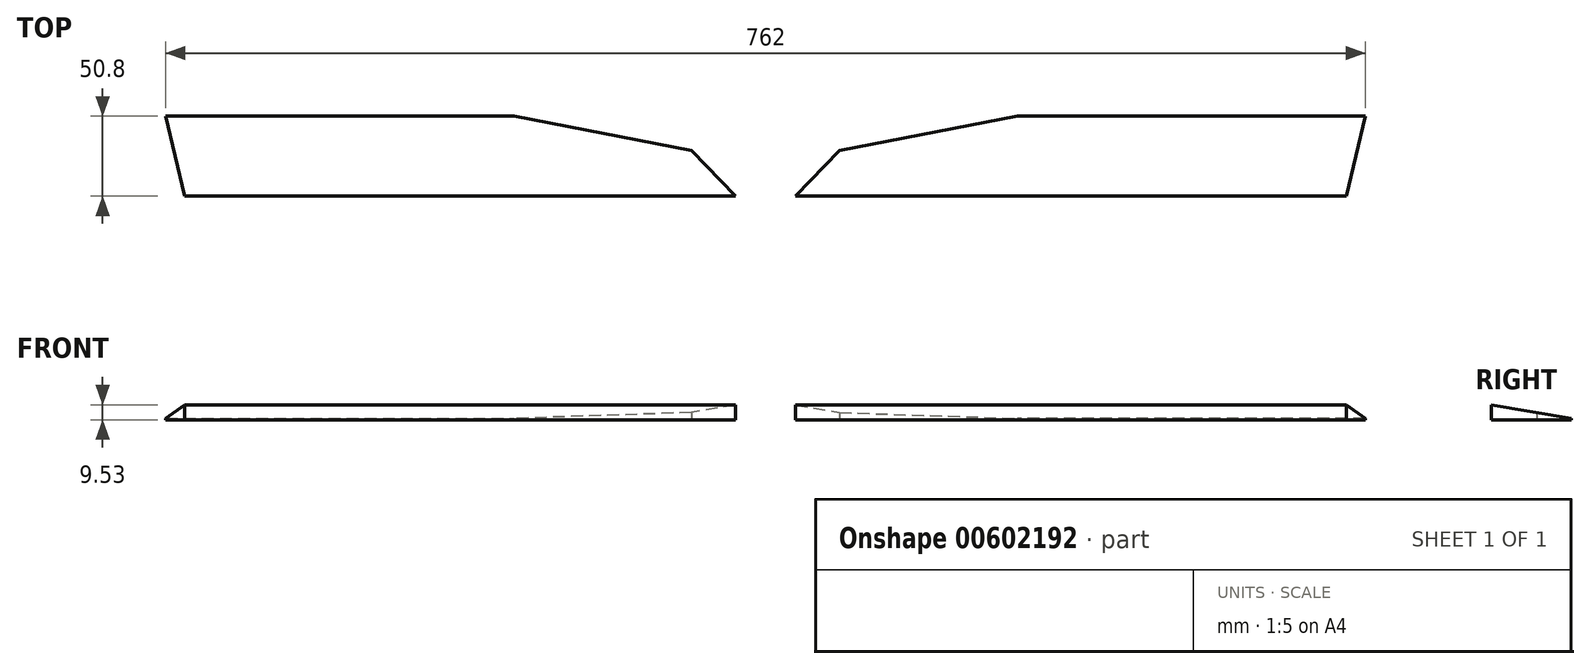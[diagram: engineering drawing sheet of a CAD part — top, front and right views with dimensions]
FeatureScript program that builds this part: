
annotation { "Feature Type Name" : "Feature", "Feature Type Description" : "" }
export const myFeature = defineFeature(function(context is Context, id is Id, definition is map)
    precondition{}
    {
        {
            var Q0;
            Q0=qCreatedBy(makeId("Right.planeOp"),FACE);
            var sketch = newSketch(context, id + "F0", { "sketchPlane" : qUnion([Q0])});
            skLineSegment(sketch, "E0", {"start": v(0, 0) * mm, "end": v(0, 9.53) * mm});
            skLineSegment(sketch, "E1.0", {"start": v(50.8, 0) * mm, "end": v(50.8, 9.53) * mm});
            skLineSegment(sketch, "E2", {"start": v(0, 0) * mm, "end": v(50.8, 0) * mm});
            skLineSegment(sketch, "E3", {"start": v(50.8, 0) * mm, "end": v(50.8, 0.78) * mm});
            skLineSegment(sketch, "E4", {"start": v(50.8, 0.78) * mm, "end": v(0, 9.53) * mm});
            skSolve(sketch);
        }
        {
            var Q0;
            Q0=makeQuery(id+"F0.imprint","IMPRINT",FACE,{"disambiguationData":[TD([[makeQuery(id+"F0.imprint","IMPRINT",EDGE,{"derivedFrom":sQuery(id+"F0.wireOp",EDGE,"E0")}),-1.0]])]});
            extrude(context, id + "F1", {"entities" : qUnion([Q0]), "depth" : 381 * mm, "offsetDistance" : 25.4 * mm});
        }
        {
            var Q0;
            Q0=qCreatedBy(makeId("Top.planeOp"),FACE);
            var sketch = newSketch(context, id + "F2", { "sketchPlane" : qUnion([Q0])});
            skLineSegment(sketch, "E5.0", {"start": v(381, 0) * mm, "end": v(0, 0) * mm});
            skLineSegment(sketch, "E6", {"start": v(381, 0) * mm, "end": v(369.06, 0) * mm});
            skLineSegment(sketch, "E7", {"start": v(369.06, 0) * mm, "end": v(381, 50.76) * mm});
            skLineSegment(sketch, "E8", {"start": v(381, 50.76) * mm, "end": v(381, 0) * mm});
            skSolve(sketch);
        }
        {
            var Q0;
            {var subQ0=sQuery(id+"F2.wireOp",EDGE,"E7");Q0=makeQuery(id+"F2.imprint","IMPRINT",FACE,{"disambiguationData":[TD([[makeQuery(id+"F2.imprint","IMPRINT",EDGE,{"derivedFrom":subQ0}),-1.0]])]});}
            extrude(context, id + "F3", {"entities" : qUnion([Q0]), "operationType" : NewBodyOperationType.REMOVE, "endBound" : BoundingType.SYMMETRIC, "depth" : 25.4 * mm, "offsetDistance" : 25.4 * mm});
        }
        {
            var Q0;
            Q0=qCreatedBy(makeId("Top.planeOp"),FACE);
            var sketch = newSketch(context, id + "F4", { "sketchPlane" : qUnion([Q0])});
            skLineSegment(sketch, "E9.1", {"start": v(19.15, 0) * mm, "end": v(0, 0) * mm});
            skLineSegment(sketch, "E9.2", {"start": v(0, 0) * mm, "end": v(0, 50.8) * mm});
            skLineSegment(sketch, "E9.3", {"start": v(159.86, 50.8) * mm, "end": v(0, 50.8) * mm});
            skLineSegment(sketch, "E10", {"start": v(19.15, 0) * mm, "end": v(47.03, 28.87) * mm});
            skLineSegment(sketch, "E11", {"start": v(47.03, 28.87) * mm, "end": v(159.86, 50.8) * mm});
            skSolve(sketch);
        }
        {
            var Q0;
            Q0=makeQuery(id+"F4.imprint","IMPRINT",FACE,{"disambiguationData":[TD([[makeQuery(id+"F4.imprint","IMPRINT",EDGE,{"derivedFrom":sQuery(id+"F4.wireOp",EDGE,"E9.1")}),-1.0]])]});
            extrude(context, id + "F5", {"entities" : qUnion([Q0]), "operationType" : NewBodyOperationType.REMOVE, "endBound" : BoundingType.SYMMETRIC, "depth" : 25.4 * mm, "offsetDistance" : 25.4 * mm});
        }
        {
            var Q0;
            Q0=makeQuery(id+"F1.opExtrude","SWEPT_BODY",BODY,{"disambiguationData":[OSD([sQuery(id+"F0.wireOp",EDGE,"E0"),sQuery(id+"F0.wireOp",EDGE,"E1.0"),sQuery(id+"F0.wireOp",EDGE,"E2"),sQuery(id+"F0.wireOp",EDGE,"E4")])]});
            var Q1;
            Q1=qCreatedBy(makeId("Right.planeOp"),FACE);
            mirror(context, id + "F6", {"entities" : qUnion([Q0]), "mirrorPlane" : qUnion([Q1])});
        }
    });
